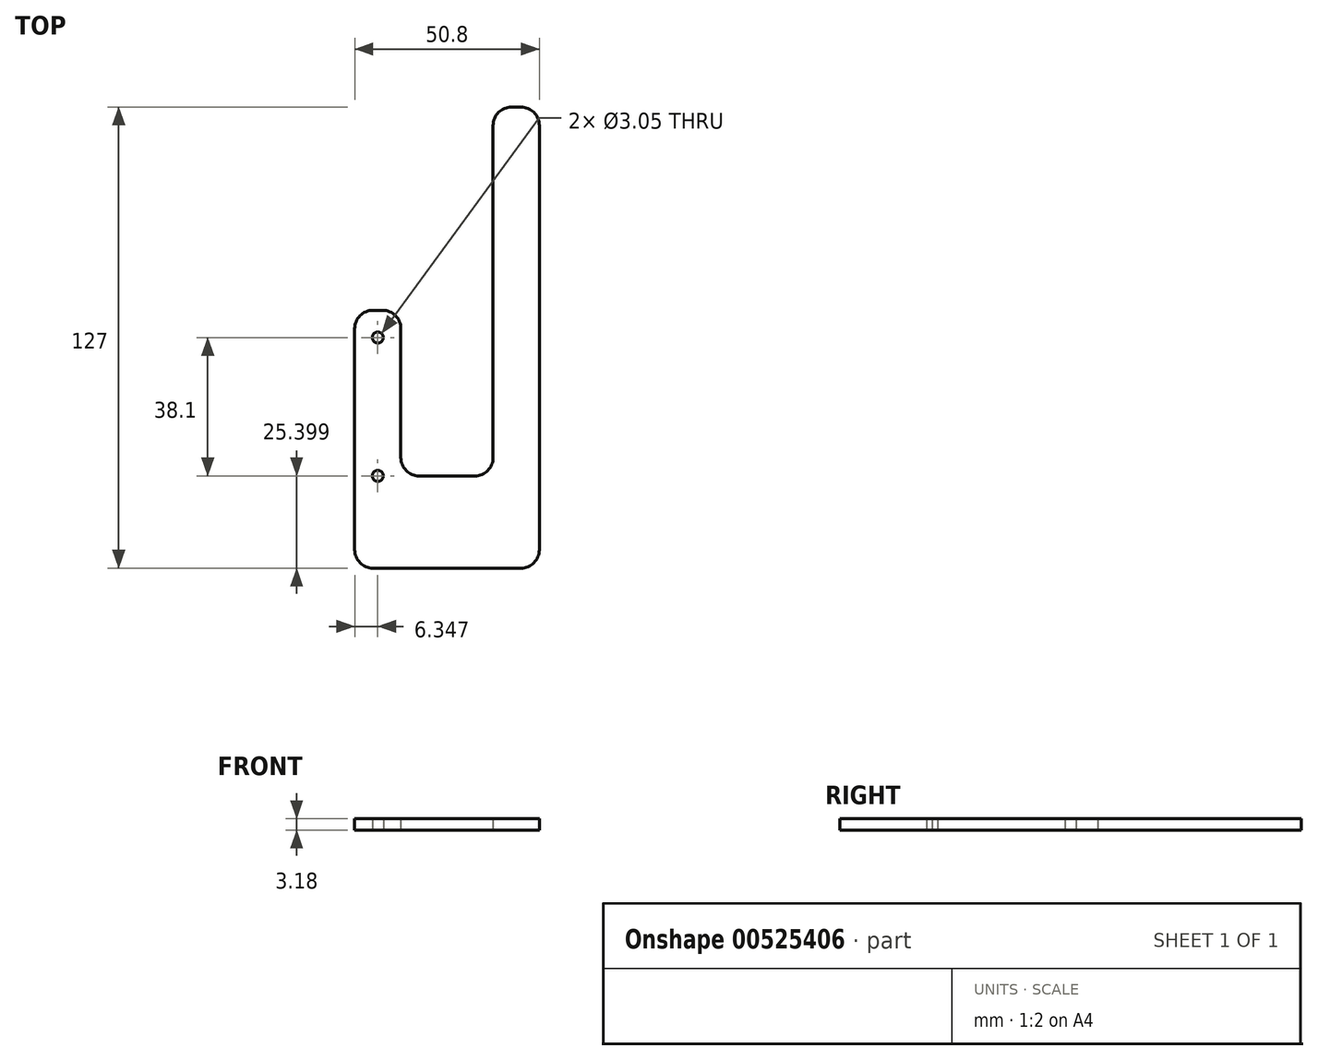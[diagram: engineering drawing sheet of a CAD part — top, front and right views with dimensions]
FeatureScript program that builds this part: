
annotation { "Feature Type Name" : "Feature", "Feature Type Description" : "" }
export const myFeature = defineFeature(function(context is Context, id is Id, definition is map)
    precondition{}
    {
        {
            var Q0;
            Q0=qCreatedBy(makeId("Top.planeOp"),FACE);
            var sketch = newSketch(context, id + "F0", { "sketchPlane" : qUnion([Q0])});
            skLineSegment(sketch, "E0.bottom", {"start": v(-24.21, -2.66) * mm, "end": v(1.19, -2.66) * mm});
            skLineSegment(sketch, "E0.top", {"start": v(-36.91, -28.06) * mm, "end": v(13.89, -28.06) * mm});
            skLineSegment(sketch, "E0.left", {"start": v(-36.91, -2.66) * mm, "end": v(-36.91, -28.06) * mm});
            skLineSegment(sketch, "E0.right", {"start": v(13.89, -2.66) * mm, "end": v(13.89, -28.06) * mm});
            skLineSegment(sketch, "E1.top", {"start": v(1.19, 73.54) * mm, "end": v(13.89, 73.54) * mm});
            skLineSegment(sketch, "E1.left", {"start": v(1.19, -2.66) * mm, "end": v(1.19, 73.54) * mm});
            skLineSegment(sketch, "E1.right", {"start": v(13.89, -12.02) * mm, "end": v(13.89, 73.54) * mm});
            skLineSegment(sketch, "E2.left", {"start": v(-24.21, -2.66) * mm, "end": v(-24.21, 42.95) * mm});
            skLineSegment(sketch, "E2.right", {"start": v(-36.91, -12.02) * mm, "end": v(-36.91, 42.95) * mm});
            skCircle(sketch, "E3", {"center": v(-30.56, -2.66) * mm, "radius": 1.52 * mm});
            skCircle(sketch, "E4", {"center": v(-30.56, 35.44) * mm, "radius": 1.52 * mm});
            skLineSegment(sketch, "E5", {"start": v(-36.91, 42.95) * mm, "end": v(-24.21, 42.95) * mm});
            skPoint(sketch, "E6.orphan", {"position": v(-36.91, 73.54) * mm});
            skLineSegment(sketch, "E7.top", {"start": v(1.19, 98.94) * mm, "end": v(13.89, 98.94) * mm});
            skLineSegment(sketch, "E7.left", {"start": v(1.19, 73.54) * mm, "end": v(1.19, 98.94) * mm});
            skLineSegment(sketch, "E7.right", {"start": v(13.89, 73.54) * mm, "end": v(13.89, 98.94) * mm});
            skSolve(sketch);
        }
        {
            var Q0;
            Q0=makeQuery(id+"F0.imprint","IMPRINT",FACE,{"disambiguationData":[TD([[makeQuery(id+"F0.imprint","IMPRINT",EDGE,{"derivedFrom":sQuery(id+"F0.wireOp",EDGE,"E0.bottom")}),-1.0]])]});
            var Q1;
            Q1=makeQuery(id+"F0.imprint","IMPRINT",FACE,{"disambiguationData":[TD([[makeQuery(id+"F0.imprint","IMPRINT",EDGE,{"derivedFrom":sQuery(id+"F0.wireOp",EDGE,"E1.top")}),1.0]])]});
            extrude(context, id + "F1", {"entities" : qUnion([Q0, Q1]), "depth" : 3.17 * mm, "offsetDistance" : 25.4 * mm});
        }
        {
            var Q0;
            Q0=makeQuery(id+"F1.opExtrude","SWEPT_EDGE",EDGE,{"disambiguationData":[OSD([sQuery(id+"F0.wireOp",EDGE,"E2.top"),sQuery(id+"F0.wireOp",EDGE,"E2.right")])]});
            var Q1;
            Q1=makeQuery(id+"F1.opExtrude","SWEPT_EDGE",EDGE,{"disambiguationData":[OSD([sQuery(id+"F0.wireOp",EDGE,"E2.top"),sQuery(id+"F0.wireOp",EDGE,"E2.left")])]});
            var Q2;
            Q2=makeQuery(id+"F1.opExtrude","SWEPT_EDGE",EDGE,{"disambiguationData":[OSD([sQuery(id+"F0.wireOp",EDGE,"E1.top"),sQuery(id+"F0.wireOp",EDGE,"E1.left")])]});
            var Q3;
            Q3=makeQuery(id+"F1.opExtrude","SWEPT_EDGE",EDGE,{"disambiguationData":[OSD([sQuery(id+"F0.wireOp",EDGE,"E1.top"),sQuery(id+"F0.wireOp",EDGE,"E1.right")])]});
            var Q4;
            Q4=makeQuery(id+"F1.opExtrude","SWEPT_EDGE",EDGE,{"disambiguationData":[OSD([sQuery(id+"F0.wireOp",EDGE,"E0.top"),sQuery(id+"F0.wireOp",EDGE,"E0.left")])]});
            var Q5;
            Q5=makeQuery(id+"F1.opExtrude","SWEPT_EDGE",EDGE,{"disambiguationData":[OSD([sQuery(id+"F0.wireOp",EDGE,"E0.top"),sQuery(id+"F0.wireOp",EDGE,"E0.right")])]});
            var Q6;
            Q6=makeQuery(id+"F1.opExtrude","SWEPT_EDGE",EDGE,{"disambiguationData":[OSD([sQuery(id+"F0.wireOp",EDGE,"E0.bottom"),sQuery(id+"F0.wireOp",EDGE,"E2.left")])]});
            var Q7;
            Q7=makeQuery(id+"F1.opExtrude","SWEPT_EDGE",EDGE,{"disambiguationData":[OSD([sQuery(id+"F0.wireOp",EDGE,"E0.bottom"),sQuery(id+"F0.wireOp",EDGE,"E1.left")])]});
            var Q8;
            Q8=makeQuery(id+"F1.opExtrude","SWEPT_EDGE",EDGE,{"disambiguationData":[OSD([sQuery(id+"F0.wireOp",EDGE,"E7.top"),sQuery(id+"F0.wireOp",EDGE,"E7.left")])]});
            var Q9;
            Q9=makeQuery(id+"F1.opExtrude","SWEPT_EDGE",EDGE,{"disambiguationData":[OSD([sQuery(id+"F0.wireOp",EDGE,"E7.top"),sQuery(id+"F0.wireOp",EDGE,"E7.right")])]});
            fillet(context, id + "F2", {"entities" : qUnion([Q0, Q1, Q2, Q3, Q4, Q5, Q6, Q7, Q8, Q9]), "radius" : 5.08 * mm, "tangentPropagation" : true, "allowEdgeOverflow" : false});
        }
    });
